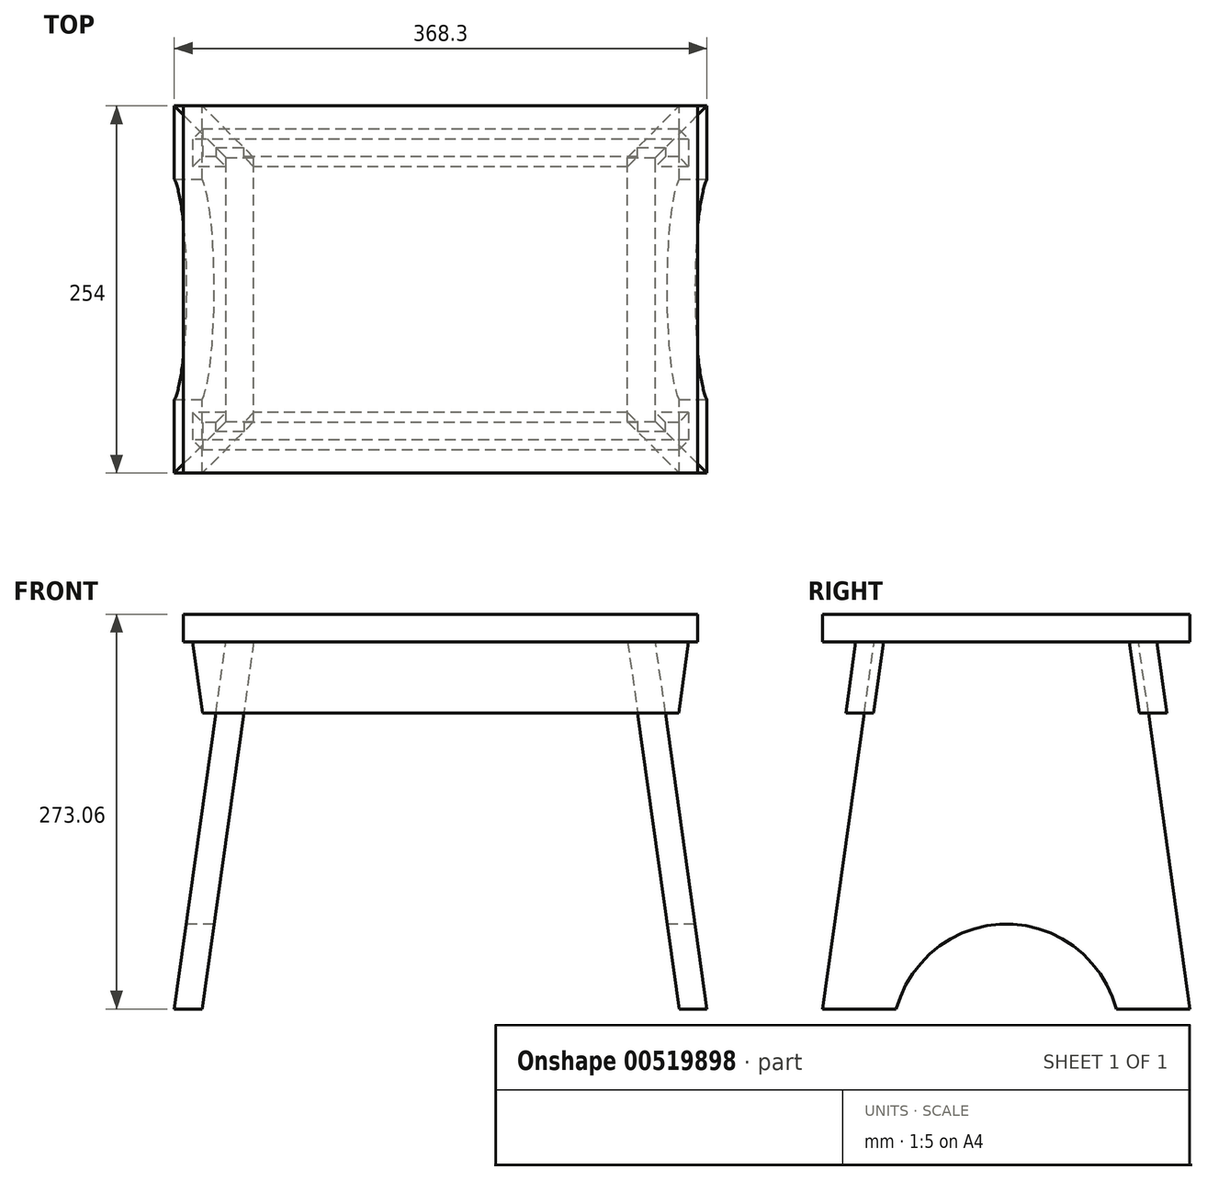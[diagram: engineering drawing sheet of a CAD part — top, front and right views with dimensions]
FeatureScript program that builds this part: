
annotation { "Feature Type Name" : "Feature", "Feature Type Description" : "" }
export const myFeature = defineFeature(function(context is Context, id is Id, definition is map)
    precondition{}
    {
        {
            var Q0;
            Q0=qCreatedBy(makeId("Front.planeOp"),FACE);
            var sketch = newSketch(context, id + "F0", { "sketchPlane" : qUnion([Q0])});
            skLineSegment(sketch, "E0.bottom", {"start": v(-177.8, 9.53) * mm, "end": v(177.8, 9.53) * mm});
            skLineSegment(sketch, "E0.top", {"start": v(-177.8, -9.53) * mm, "end": v(177.8, -9.53) * mm});
            skLineSegment(sketch, "E0.left", {"start": v(-177.8, 9.53) * mm, "end": v(-177.8, -9.52) * mm});
            skLineSegment(sketch, "E0.right", {"start": v(177.8, 9.53) * mm, "end": v(177.8, -9.52) * mm});
            skPoint(sketch, "E0.middle", {"position": v(0, 0) * mm});
            skLineSegment(sketch, "E1.bottom", {"start": v(-177.8, -9.53) * mm, "end": v(177.8, -9.53) * mm, "construction": true});
            skLineSegment(sketch, "E1.top", {"start": v(-177.8, -263.53) * mm, "end": v(177.8, -263.52) * mm, "construction": true});
            skLineSegment(sketch, "E1.left", {"start": v(-177.8, -9.53) * mm, "end": v(-177.8, -263.53) * mm, "construction": true});
            skLineSegment(sketch, "E1.right", {"start": v(177.8, -9.53) * mm, "end": v(177.8, -263.52) * mm, "construction": true});
            skLineSegment(sketch, "E2", {"start": v(148.45, -9.53) * mm, "end": v(184.15, -263.53) * mm});
            skLineSegment(sketch, "E3", {"start": v(164.91, -263.53) * mm, "end": v(129.22, -9.52) * mm});
            skLineSegment(sketch, "E4", {"start": v(164.91, -263.53) * mm, "end": v(184.15, -263.53) * mm});
            skLineSegment(sketch, "E5", {"start": v(0, 0) * mm, "end": v(0, -263.53) * mm, "construction": true});
            skLineSegment(sketch, "E6.MirrorCS", {"start": v(-164.91, -263.53) * mm, "end": v(-129.22, -9.53) * mm});
            skLineSegment(sketch, "E7.MirrorCS", {"start": v(-148.45, -9.52) * mm, "end": v(-184.15, -263.53) * mm});
            skLineSegment(sketch, "E8", {"start": v(-164.91, -263.53) * mm, "end": v(-184.15, -263.53) * mm});
            skLineSegment(sketch, "E9.top", {"start": v(-177.8, -58.8) * mm, "end": v(177.8, -58.8) * mm});
            skLineSegment(sketch, "E9.left", {"start": v(-177.8, -9.53) * mm, "end": v(-177.8, -58.8) * mm});
            skLineSegment(sketch, "E9.right", {"start": v(177.8, -9.53) * mm, "end": v(177.8, -58.8) * mm});
            skLineSegment(sketch, "E10", {"start": v(171.45, -9.52) * mm, "end": v(164.52, -58.8) * mm});
            skLineSegment(sketch, "E11.MirrorCS", {"start": v(-171.45, -9.53) * mm, "end": v(-164.52, -58.8) * mm});
            skSolve(sketch);
        }
        {
            var Q0;
            Q0=makeQuery(id+"F0.imprint","IMPRINT",FACE,{"disambiguationData":[TD([[makeQuery(id+"F0.imprint","IMPRINT",EDGE,{"derivedFrom":sQuery(id+"F0.wireOp",EDGE,"E0.bottom")}),-1.0]])]});
            extrude(context, id + "F1", {"entities" : qUnion([Q0]), "endBound" : BoundingType.SYMMETRIC, "depth" : 254 * mm, "offsetDistance" : 25.4 * mm});
        }
        {
            var Q0;
            {var subQ0=sQuery(id+"F0.wireOp",EDGE,"E8");Q0=makeQuery(id+"F0.imprint","IMPRINT",FACE,{"disambiguationData":[TD([[makeQuery(id+"F0.imprint","IMPRINT",EDGE,{"derivedFrom":subQ0}),-1.0]])]});}
            var Q1;
            {var subQ0=sQuery(id+"F0.wireOp",EDGE,"E0.top");var subQ1=sQuery(id+"F0.wireOp",EDGE,"E6.MirrorCS");var subQ2=makeQuery(id+"F0.imprint","INTERSECT",VERTEX,{"derivedFrom":[subQ1,subQ0]});Q1=makeQuery(id+"F0.imprint","IMPRINT",FACE,{"disambiguationData":[TD([[makeQuery(id+"F0.imprint","IMPRINT",EDGE,{"disambiguationData":[TD([[subQ2,1.0]])],"derivedFrom":subQ1}),1.0]])]});}
            var Q2;
            {var subQ0=sQuery(id+"F0.wireOp",EDGE,"E0.top");var subQ1=sQuery(id+"F0.wireOp",EDGE,"E2");var subQ2=makeQuery(id+"F0.imprint","INTERSECT",VERTEX,{"derivedFrom":[subQ1,subQ0]});Q2=makeQuery(id+"F0.imprint","IMPRINT",FACE,{"disambiguationData":[TD([[makeQuery(id+"F0.imprint","IMPRINT",EDGE,{"disambiguationData":[TD([[subQ2,-1.0]])],"derivedFrom":subQ1}),-1.0]])]});}
            var Q3;
            {var subQ0=sQuery(id+"F0.wireOp",EDGE,"E4");Q3=makeQuery(id+"F0.imprint","IMPRINT",FACE,{"disambiguationData":[TD([[makeQuery(id+"F0.imprint","IMPRINT",EDGE,{"derivedFrom":subQ0}),1.0]])]});}
            var Q4;
            Q4=makeQuery(id+"F1.opExtrude","CAP_VERTEX",VERTEX,{"disambiguationData":[OSD([sQuery(id+"F0.wireOp",EDGE,"E0.right"),sQuery(id+"F0.wireOp",EDGE,"E0.top"),sQuery(id+"F0.wireOp",EDGE,"E9.right")])],"isStart":false});
            var Q5;
            Q5=makeQuery(id+"F1.opExtrude","CAP_VERTEX",VERTEX,{"disambiguationData":[OSD([sQuery(id+"F0.wireOp",EDGE,"E0.right"),sQuery(id+"F0.wireOp",EDGE,"E0.top"),sQuery(id+"F0.wireOp",EDGE,"E9.right")])],"isStart":true});
            extrude(context, id + "F2", {"entities" : qUnion([Q0, Q1, Q2, Q3]), "endBound" : BoundingType.UP_TO_VERTEX, "depth" : mm, "endBoundEntityVertex" : qUnion([Q4]), "offsetDistance" : 25.4 * mm, "hasSecondDirection" : true, "secondDirectionBound" : SecondDirectionBoundingType.UP_TO_VERTEX, "secondDirectionOppositeDirection" : true, "secondDirectionDepth" : 25.4 * mm, "secondDirectionBoundEntityVertex" : qUnion([Q5])});
        }
        {
            var Q0;
            Q0=qCreatedBy(makeId("Right.planeOp"),FACE);
            var sketch = newSketch(context, id + "F3", { "sketchPlane" : qUnion([Q0])});
            skLineSegment(sketch, "E12.0.0", {"start": v(127, -9.53) * mm, "end": v(-127, -9.53) * mm});
            skLineSegment(sketch, "E12.0.1", {"start": v(-127, -9.53) * mm, "end": v(-127, -263.53) * mm});
            skLineSegment(sketch, "E12.0.3", {"start": v(127, -263.53) * mm, "end": v(127, -9.53) * mm});
            skLineSegment(sketch, "E13", {"start": v(-127, -263.53) * mm, "end": v(-91.3, -9.52) * mm});
            skLineSegment(sketch, "E14.MirrorCS", {"start": v(127, -263.53) * mm, "end": v(91.3, -9.52) * mm});
            skPoint(sketch, "E15.end.orphan", {"position": v(0, -263.53) * mm});
            skLineSegment(sketch, "E16", {"start": v(-127, -263.53) * mm, "end": v(-76.2, -263.53) * mm});
            skLineSegment(sketch, "E17", {"start": v(127, -263.53) * mm, "end": v(76.2, -263.53) * mm});
            skArc(sketch, "E18", {"start": v(76.2, -263.53) * mm, "mid": v(0, -204.6) * mm, "end": v(-76.2, -263.53) * mm});
            skLineSegment(sketch, "E19", {"start": v(-76.2, -263.53) * mm, "end": v(76.2, -263.53) * mm});
            skSolve(sketch);
        }
        {
            var Q0;
            {var subQ0=sQuery(id+"F3.wireOp",EDGE,"E12.0.1");Q0=makeQuery(id+"F3.imprint","IMPRINT",FACE,{"disambiguationData":[TD([[makeQuery(id+"F3.imprint","IMPRINT",EDGE,{"derivedFrom":subQ0}),1.0]])]});}
            var Q1;
            {var subQ0=sQuery(id+"F3.wireOp",EDGE,"E12.0.3");Q1=makeQuery(id+"F3.imprint","IMPRINT",FACE,{"disambiguationData":[TD([[makeQuery(id+"F3.imprint","IMPRINT",EDGE,{"derivedFrom":subQ0}),1.0]])]});}
            var Q2;
            Q2=makeQuery(id+"F3.imprint","IMPRINT",FACE,{"disambiguationData":[TD([[makeQuery(id+"F3.imprint","IMPRINT",EDGE,{"derivedFrom":sQuery(id+"F3.wireOp",EDGE,"E18")}),1.0]])]});
            extrude(context, id + "F4", {"entities" : qUnion([Q0, Q1, Q2]), "operationType" : NewBodyOperationType.REMOVE, "endBound" : BoundingType.THROUGH_ALL, "oppositeDirection" : true, "depth" : 25.4 * mm, "offsetDistance" : 25.4 * mm, "hasSecondDirection" : true, "secondDirectionBound" : SecondDirectionBoundingType.THROUGH_ALL, "secondDirectionOppositeDirection" : false, "secondDirectionDepth" : 25.4 * mm});
        }
        {
            var Q0;
            Q0=qCreatedBy(makeId("Right.planeOp"),FACE);
            var sketch = newSketch(context, id + "F5", { "sketchPlane" : qUnion([Q0])});
            skLineSegment(sketch, "E20.0.0", {"start": v(127, -263.52) * mm, "end": v(91.3, -9.52) * mm});
            skLineSegment(sketch, "E20.0.1", {"start": v(91.3, -9.53) * mm, "end": v(-91.3, -9.53) * mm});
            skLineSegment(sketch, "E20.0.2", {"start": v(-91.3, -9.53) * mm, "end": v(-127, -263.53) * mm});
            skLineSegment(sketch, "E20.0.3", {"start": v(-127, -263.53) * mm, "end": v(-76.2, -263.53) * mm});
            skLineSegment(sketch, "E20.0.5", {"start": v(76.2, -263.53) * mm, "end": v(127, -263.53) * mm});
            skLineSegment(sketch, "E21.0", {"start": v(-127, -9.53) * mm, "end": v(127, -9.53) * mm});
            skLineSegment(sketch, "E22", {"start": v(-104.13, -9.53) * mm, "end": v(-111.05, -58.8) * mm});
            skLineSegment(sketch, "E23", {"start": v(-111.05, -58.8) * mm, "end": v(-91.82, -58.8) * mm});
            skLineSegment(sketch, "E24", {"start": v(-91.82, -58.8) * mm, "end": v(-84.9, -9.53) * mm});
            skLineSegment(sketch, "E25", {"start": v(-84.9, -9.53) * mm, "end": v(-104.13, -9.53) * mm});
            skLineSegment(sketch, "E26", {"start": v(-91.82, -58.8) * mm, "end": v(0, -58.8) * mm, "construction": true});
            skLineSegment(sketch, "E27.MirrorCS", {"start": v(104.13, -9.53) * mm, "end": v(111.05, -58.8) * mm});
            skLineSegment(sketch, "E28.MirrorCS", {"start": v(111.05, -58.8) * mm, "end": v(91.82, -58.8) * mm});
            skLineSegment(sketch, "E29.MirrorCS", {"start": v(91.82, -58.8) * mm, "end": v(84.9, -9.53) * mm});
            skLineSegment(sketch, "E30.MirrorCS", {"start": v(84.9, -9.53) * mm, "end": v(104.13, -9.53) * mm});
            skLineSegment(sketch, "E31.0.0", {"start": v(127, -9.53) * mm, "end": v(127, 9.53) * mm});
            skLineSegment(sketch, "E31.0.1", {"start": v(127, 9.53) * mm, "end": v(-127, 9.53) * mm});
            skLineSegment(sketch, "E31.0.2", {"start": v(-127, 9.53) * mm, "end": v(-127, -9.53) * mm});
            skLineSegment(sketch, "E32", {"start": v(0, 0) * mm, "end": v(0, -58.8) * mm, "construction": true});
            skArc(sketch, "E33", {"start": v(76.2, -263.53) * mm, "mid": v(0, -193.47) * mm, "end": v(-76.2, -263.53) * mm});
            skSolve(sketch);
        }
        {
            var Q0;
            {var subQ5=sQuery(id+"F5.wireOp",EDGE,"E22");Q0=makeQuery(id+"F5.imprint","IMPRINT",FACE,{"disambiguationData":[TD([[makeQuery(id+"F5.imprint","IMPRINT",EDGE,{"derivedFrom":subQ5}),1.0]])]});}
            var Q1;
            {var subQ5=sQuery(id+"F5.wireOp",EDGE,"E24");Q1=makeQuery(id+"F5.imprint","IMPRINT",FACE,{"disambiguationData":[TD([[makeQuery(id+"F5.imprint","IMPRINT",EDGE,{"derivedFrom":subQ5}),1.0]])]});}
            var Q2;
            {var subQ5=sQuery(id+"F5.wireOp",EDGE,"E29.MirrorCS");Q2=makeQuery(id+"F5.imprint","IMPRINT",FACE,{"disambiguationData":[TD([[makeQuery(id+"F5.imprint","IMPRINT",EDGE,{"derivedFrom":subQ5}),-1.0]])]});}
            var Q3;
            {var subQ5=sQuery(id+"F5.wireOp",EDGE,"E27.MirrorCS");Q3=makeQuery(id+"F5.imprint","IMPRINT",FACE,{"disambiguationData":[TD([[makeQuery(id+"F5.imprint","IMPRINT",EDGE,{"derivedFrom":subQ5}),-1.0]])]});}
            var Q4;
            Q4=makeQuery(id+"F1.opExtrude","SWEPT_FACE",FACE,{"disambiguationData":[OSD([sQuery(id+"F0.wireOp",EDGE,"E0.right")])]});
            var Q5;
            Q5=makeQuery(id+"F1.opExtrude","SWEPT_FACE",FACE,{"disambiguationData":[OSD([sQuery(id+"F0.wireOp",EDGE,"E0.left")])]});
            extrude(context, id + "F6", {"entities" : qUnion([Q0, Q1, Q2, Q3]), "endBound" : BoundingType.UP_TO_SURFACE, "depth" : 25.4 * mm, "endBoundEntityFace" : qUnion([Q4]), "offsetDistance" : 25.4 * mm, "hasSecondDirection" : true, "secondDirectionBound" : SecondDirectionBoundingType.UP_TO_SURFACE, "secondDirectionOppositeDirection" : true, "secondDirectionDepth" : 25.4 * mm, "secondDirectionBoundEntityFace" : qUnion([Q5])});
        }
        {
            var Q0;
            {var subQ0=sQuery(id+"F0.wireOp",EDGE,"E9.right");Q0=makeQuery(id+"F0.imprint","IMPRINT",FACE,{"disambiguationData":[TD([[makeQuery(id+"F0.imprint","IMPRINT",EDGE,{"derivedFrom":subQ0}),-1.0]])]});}
            var Q1;
            {var subQ0=sQuery(id+"F0.wireOp",EDGE,"E9.left");Q1=makeQuery(id+"F0.imprint","IMPRINT",FACE,{"disambiguationData":[TD([[makeQuery(id+"F0.imprint","IMPRINT",EDGE,{"derivedFrom":subQ0}),1.0]])]});}
            extrude(context, id + "F7", {"entities" : qUnion([Q0, Q1]), "operationType" : NewBodyOperationType.REMOVE, "endBound" : BoundingType.THROUGH_ALL, "oppositeDirection" : true, "depth" : 25.4 * mm, "offsetDistance" : 25.4 * mm, "hasSecondDirection" : true, "secondDirectionBound" : SecondDirectionBoundingType.THROUGH_ALL, "secondDirectionOppositeDirection" : false, "secondDirectionDepth" : 25.4 * mm});
        }
        {
            var Q0;
            Q0=makeQuery(id+"F2.opExtrude","SWEPT_BODY",BODY,{"disambiguationData":[OSD([sQuery(id+"F0.wireOp",EDGE,"E6.MirrorCS"),sQuery(id+"F0.wireOp",EDGE,"E7.MirrorCS"),sQuery(id+"F0.wireOp",EDGE,"E8"),sQuery(id+"F0.wireOp",EDGE,"E0.top")])]});
            var Q1;
            Q1=makeQuery(id+"F2.opExtrude","SWEPT_BODY",BODY,{"disambiguationData":[OSD([sQuery(id+"F0.wireOp",EDGE,"E2"),sQuery(id+"F0.wireOp",EDGE,"E3"),sQuery(id+"F0.wireOp",EDGE,"E4"),sQuery(id+"F0.wireOp",EDGE,"E0.top")])]});
            var Q2;
            Q2=makeQuery(id+"F6.opExtrude","SWEPT_BODY",BODY,{"disambiguationData":[OSD([sQuery(id+"F5.wireOp",EDGE,"E22"),sQuery(id+"F5.wireOp",EDGE,"E23"),sQuery(id+"F5.wireOp",EDGE,"E24"),sQuery(id+"F5.wireOp",EDGE,"E21.0")])]});
            var Q3;
            Q3=makeQuery(id+"F6.opExtrude","SWEPT_BODY",BODY,{"disambiguationData":[OSD([sQuery(id+"F5.wireOp",EDGE,"E27.MirrorCS"),sQuery(id+"F5.wireOp",EDGE,"E28.MirrorCS"),sQuery(id+"F5.wireOp",EDGE,"E29.MirrorCS"),sQuery(id+"F5.wireOp",EDGE,"E21.0")])]});
            booleanBodies(context, id + "F8", {"operationType" : BooleanOperationType.SUBTRACTION, "tools" : qUnion([Q0, Q1]), "targets" : qUnion([Q2, Q3]), "keepTools" : true});
        }
    });
